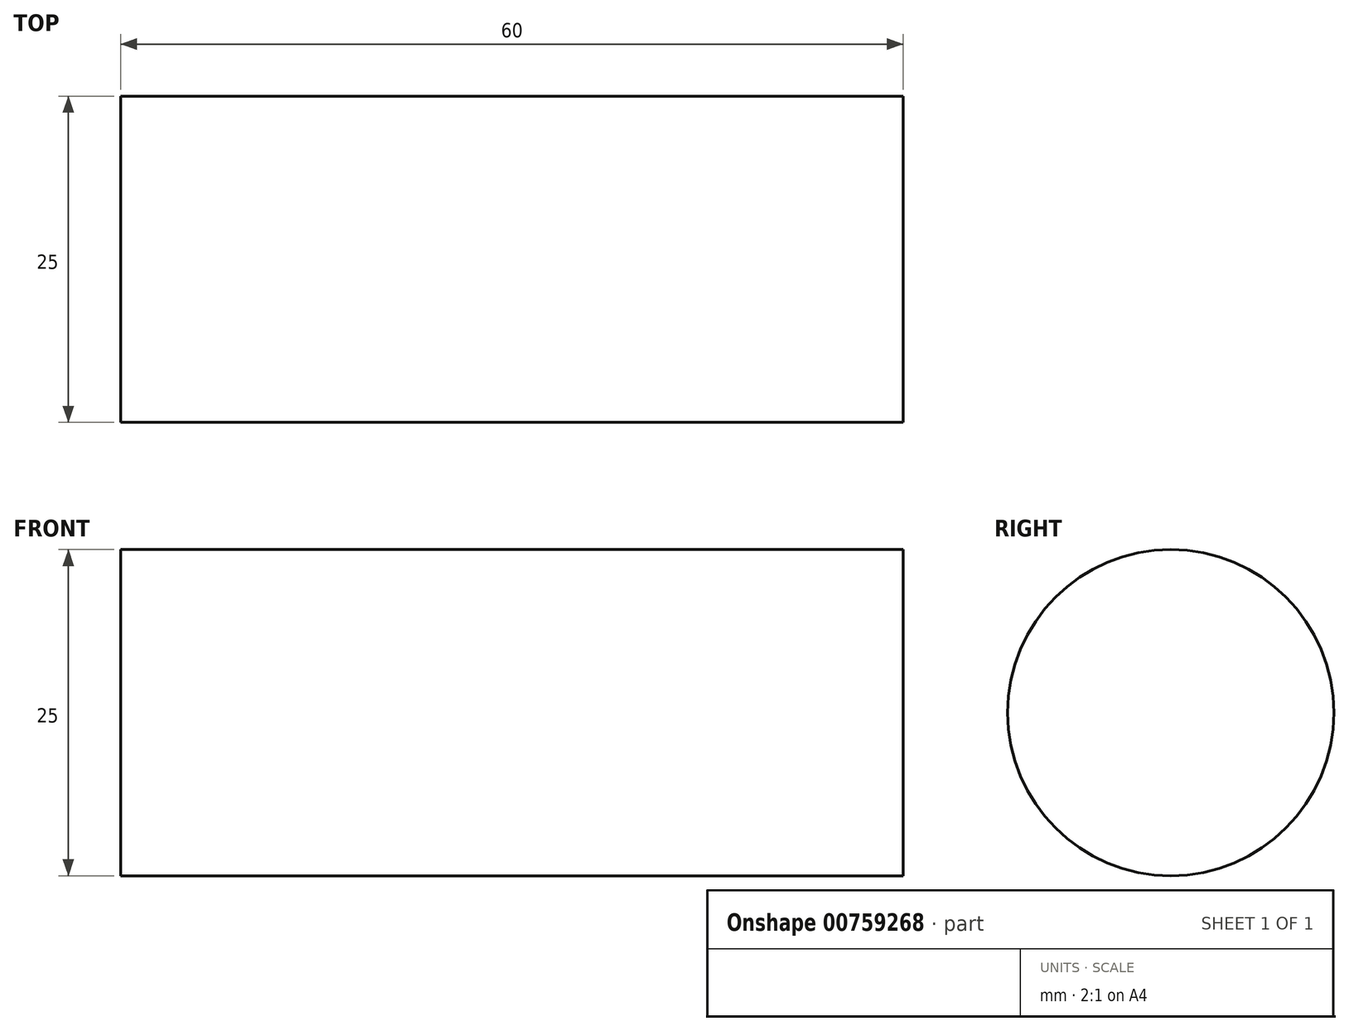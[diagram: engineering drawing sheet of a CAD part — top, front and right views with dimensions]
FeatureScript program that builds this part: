
annotation { "Feature Type Name" : "Feature", "Feature Type Description" : "" }
export const myFeature = defineFeature(function(context is Context, id is Id, definition is map)
    precondition{}
    {
        {
            var Q0;
            Q0=qCreatedBy(makeId("Right.planeOp"),FACE);
            var sketch = newSketch(context, id + "F0", { "sketchPlane" : qUnion([Q0])});
            skCircle(sketch, "E0", {"center": v(0, 0) * mm, "radius": 12.5 * mm});
            skSolve(sketch);
        }
        {
            var Q0;
            Q0 = qSketchRegion(id + "F0", true);
            extrude(context, id + "F1", {"entities" : qUnion([Q0]), "depth" : 60 * mm, "offsetDistance" : 25.4 * mm});
        }
    });
